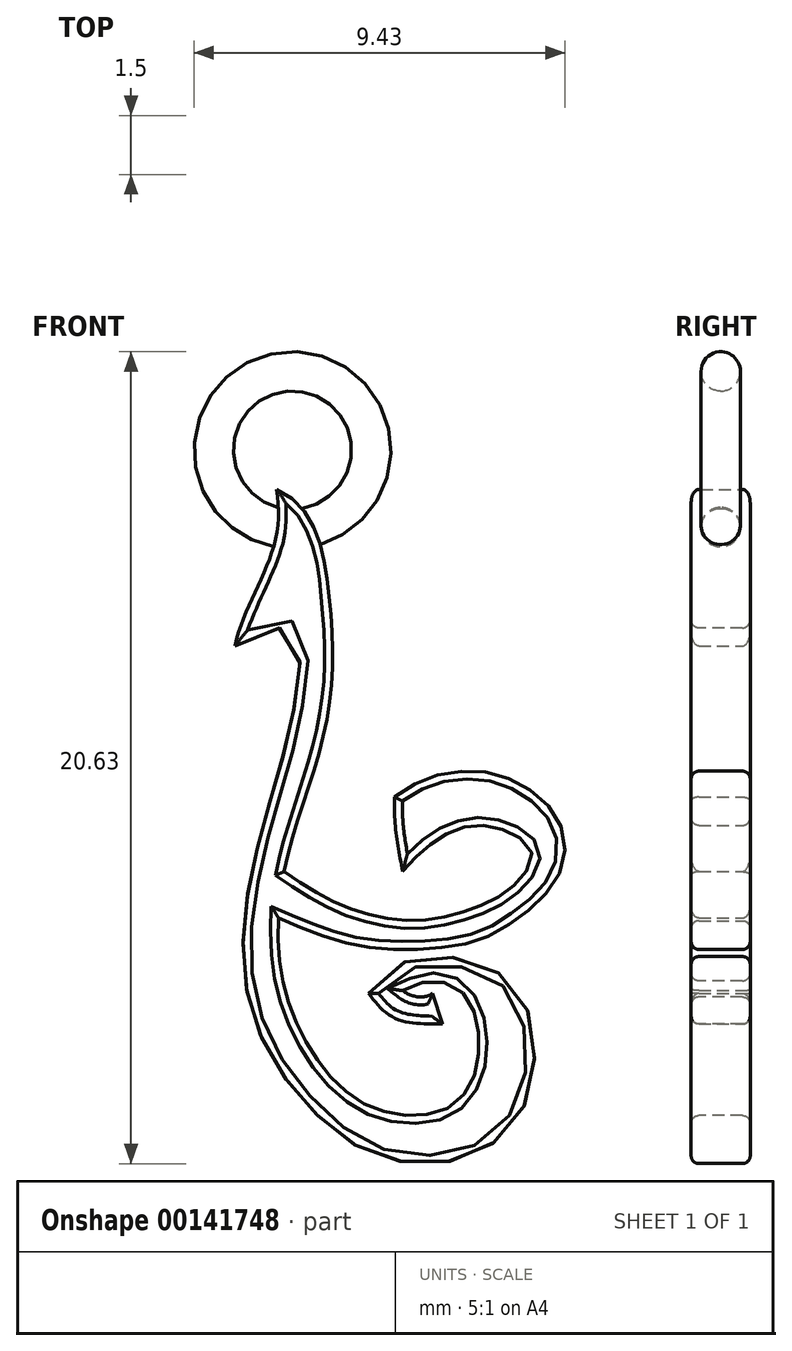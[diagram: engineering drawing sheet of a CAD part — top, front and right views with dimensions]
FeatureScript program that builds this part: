
annotation { "Feature Type Name" : "Feature", "Feature Type Description" : "" }
export const myFeature = defineFeature(function(context is Context, id is Id, definition is map)
    precondition{}
    {
        {
            var Q0;
            Q0=qCreatedBy(makeId("Front.planeOp"),FACE);
            var sketch = newSketch(context, id + "F0", { "sketchPlane" : qUnion([Q0])});
            skLineSegment(sketch, "E0.bottom", {"start": v(-7.5, 0) * mm, "end": v(9.5, 0) * mm, "construction": true});
            skLineSegment(sketch, "E0.top", {"start": v(-7.5, 17) * mm, "end": v(9.5, 17) * mm, "construction": true});
            skLineSegment(sketch, "E0.left", {"start": v(-7.5, 0) * mm, "end": v(-7.5, 17) * mm, "construction": true});
            skLineSegment(sketch, "E0.right", {"start": v(9.5, 0) * mm, "end": v(9.5, 17) * mm, "construction": true});
            skLineSegment(sketch, "E1", {"start": v(0, 0) * mm, "end": v(0, 23.23) * mm, "construction": true});
            skLineSegment(sketch, "E2", {"start": v(2.11, 3.42) * mm, "end": v(1.86, 4.2) * mm});
            skFitSpline(sketch, "E3", {"points": [v(1.86, 4.2) * mm, v(1.1, 4.27) * mm], "startDerivative": vector(-0.68, -0.46) * mm, "endDerivative": vector(-0.68, 0.54) * mm});
            skFitSpline(sketch, "E4", {"points": [v(1.1, 4.27) * mm, v(1.6, 4.48) * mm, v(2.23, 4.46) * mm, v(2.83, 3.93) * mm, v(3.04, 2.91) * mm, v(2.87, 1.98) * mm, v(2.32, 1.32) * mm, v(1.42, 1.1) * mm, v(0.23, 1.34) * mm, v(-0.95, 2.35) * mm, v(-1.8, 3.96) * mm, v(-2.06, 5.52) * mm, v(-1.91, 7.29) * mm, v(-1.38, 9.13) * mm, v(-0.76, 11.56) * mm, v(-0.75, 14.1) * mm, v(-1.06, 15.82) * mm, v(-1.44, 16.5) * mm, v(-2.1, 17) * mm], "startDerivative": vector(23.92, 10.43) * mm, "endDerivative": vector(-24, 9.9) * mm});
            skFitSpline(sketch, "E5", {"points": [v(-1.91, 7.29) * mm, v(-0.55, 6.48) * mm, v(1.22, 6.04) * mm, v(2.68, 6.28) * mm, v(3.76, 6.8) * mm, v(4.4, 7.67) * mm, v(4.1, 8.14) * mm, v(3.43, 8.42) * mm, v(2.66, 8.42) * mm, v(1.7, 7.91) * mm, v(1.1, 7.3) * mm], "startDerivative": vector(12.7, -8.61) * mm, "endDerivative": vector(-6.05, -7.17) * mm});
            skFitSpline(sketch, "E6", {"points": [v(1.1, 7.3) * mm, v(0.9, 9.19) * mm], "startDerivative": vector(-0.46, 2.24) * mm, "endDerivative": vector(0.08, 1.5) * mm});
            skFitSpline(sketch, "E7", {"points": [v(-2.05, 6.11) * mm, v(-0.62, 5.55) * mm, v(0.65, 5.33) * mm, v(2.15, 5.37) * mm, v(3.39, 5.7) * mm, v(4.57, 6.55) * mm, v(5.04, 7.15) * mm, v(5.22, 7.9) * mm, v(4.96, 8.76) * mm, v(3.99, 9.56) * mm, v(2.88, 9.84) * mm, v(1.66, 9.64) * mm, v(0.9, 9.19) * mm], "startDerivative": vector(15.2, -6.57) * mm, "endDerivative": vector(-9.55, -6.77) * mm});
            skFitSpline(sketch, "E8", {"points": [v(-2.1, 17) * mm, v(-2.1, 15.83) * mm, v(-2.63, 14.44) * mm, v(-3.16, 13.02) * mm], "startDerivative": vector(0.45, -3.7) * mm, "endDerivative": vector(-0.8, -3.86) * mm});
            skFitSpline(sketch, "E9", {"points": [v(-3.16, 13.02) * mm, v(-2.25, 13.44) * mm, v(-1.67, 13.4) * mm, v(-1.5, 12.7) * mm, v(-1.85, 10.56) * mm, v(-2.67, 7.58) * mm, v(-2.87, 4.3) * mm, v(-1.73, 1.84) * mm, v(-0.34, 0.5) * mm, v(0.5, 0.07) * mm, v(1.81, -0.13) * mm, v(3.3, 0.32) * mm, v(4.3, 1.6) * mm, v(4.37, 3.39) * mm, v(3.84, 4.47) * mm, v(2.78, 5.03) * mm, v(1.66, 5.11) * mm, v(0.76, 4.78) * mm, v(0.24, 4.2) * mm], "startDerivative": vector(20.67, 12.54) * mm, "endDerivative": vector(-11.13, -14.7) * mm});
            skCircle(sketch, "E10", {"center": v(-0.72, 7.65) * mm, "radius": 0.4 * mm, "construction": true});
            skFitSpline(sketch, "E11", {"points": [v(0.24, 4.2) * mm, v(2.11, 3.42) * mm], "startDerivative": vector(1.36, -1.73) * mm, "endDerivative": vector(3.89, 0.05) * mm});
            skSolve(sketch);
        }
        {
            var Q0;
            Q0 = qSketchRegion(id + "F0", true);
            extrude(context, id + "F1", {"entities" : qUnion([Q0]), "depth" : 1.5 * mm});
        }
        {
            var Q0;
            Q0=qCreatedBy(makeId("Right.planeOp"),FACE);
            cPlane(context, id + "F2", {"entities" : qUnion([Q0]), "cplaneType" : CPlaneType.OFFSET, "offset" : 1.7 * mm, "oppositeDirection" : true, "width" : 150 * mm, "height" : 150 * mm});
        }
        {
            var Q0;
            Q0=qCreatedBy(id+"F2.planeOp",FACE);
            var sketch = newSketch(context, id + "F3", { "sketchPlane" : qUnion([Q0])});
            skCircle(sketch, "E12", {"center": v(-0.75, 16) * mm, "radius": 0.5 * mm});
            skLineSegment(sketch, "E13", {"start": v(-3.17, 18) * mm, "end": v(2.9, 18) * mm, "construction": true});
            skSolve(sketch);
        }
        {
            var Q0;
            Q0 = qSketchRegion(id + "F3", true);
            var Q1;
            Q1=sQuery(id+"F3.wireOp",EDGE,"E13");
            revolve(context, id + "F4", {"operationType" : NewBodyOperationType.ADD, "entities" : qUnion([Q0]), "axis" : qUnion([Q1]), "revolveType" : RevolveType.FULL});
        }
        {
            var Q0;
            Q0=makeQuery(id+"F1.opExtrude","CAP_EDGE",EDGE,{"disambiguationData":[OSD([sQuery(id+"F0.wireOp",EDGE,"E5")])],"isStart":true});
            var Q1;
            Q1=makeQuery(id+"F1.opExtrude","CAP_EDGE",EDGE,{"disambiguationData":[OSD([sQuery(id+"F0.wireOp",EDGE,"E7")])],"isStart":true});
            var Q2;
            Q2=makeQuery(id+"F1.opExtrude","CAP_EDGE",EDGE,{"disambiguationData":[OSD([sQuery(id+"F0.wireOp",EDGE,"E2")])],"isStart":true});
            var Q3;
            Q3=makeQuery(id+"F1.opExtrude","CAP_EDGE",EDGE,{"disambiguationData":[OSD([sQuery(id+"F0.wireOp",EDGE,"E4")])],"isStart":true});
            var Q4;
            Q4=makeQuery(id+"F1.opExtrude","CAP_FACE",FACE,{"disambiguationData":[OSD([sQuery(id+"F0.wireOp",EDGE,"E2"),sQuery(id+"F0.wireOp",EDGE,"E3"),sQuery(id+"F0.wireOp",EDGE,"E4"),sQuery(id+"F0.wireOp",EDGE,"E5"),sQuery(id+"F0.wireOp",EDGE,"E6"),sQuery(id+"F0.wireOp",EDGE,"E7"),sQuery(id+"F0.wireOp",EDGE,"E8"),sQuery(id+"F0.wireOp",EDGE,"E9"),sQuery(id+"F0.wireOp",EDGE,"E11"),sQuery(id+"F0.wireOp",EDGE,"E4")])],"isStart":true});
            var Q5;
            Q5=makeQuery(id+"F1.opExtrude","CAP_FACE",FACE,{"disambiguationData":[OSD([sQuery(id+"F0.wireOp",EDGE,"E2"),sQuery(id+"F0.wireOp",EDGE,"E3"),sQuery(id+"F0.wireOp",EDGE,"E4"),sQuery(id+"F0.wireOp",EDGE,"E5"),sQuery(id+"F0.wireOp",EDGE,"E6"),sQuery(id+"F0.wireOp",EDGE,"E7"),sQuery(id+"F0.wireOp",EDGE,"E8"),sQuery(id+"F0.wireOp",EDGE,"E9"),sQuery(id+"F0.wireOp",EDGE,"E11"),sQuery(id+"F0.wireOp",EDGE,"E4")])],"isStart":false});
            fillet(context, id + "F5", {"entities" : qUnion([Q0, Q1, Q2, Q3, Q4, Q5]), "radius" : 0.2 * mm, "allowEdgeOverflow" : false});
        }
    });
